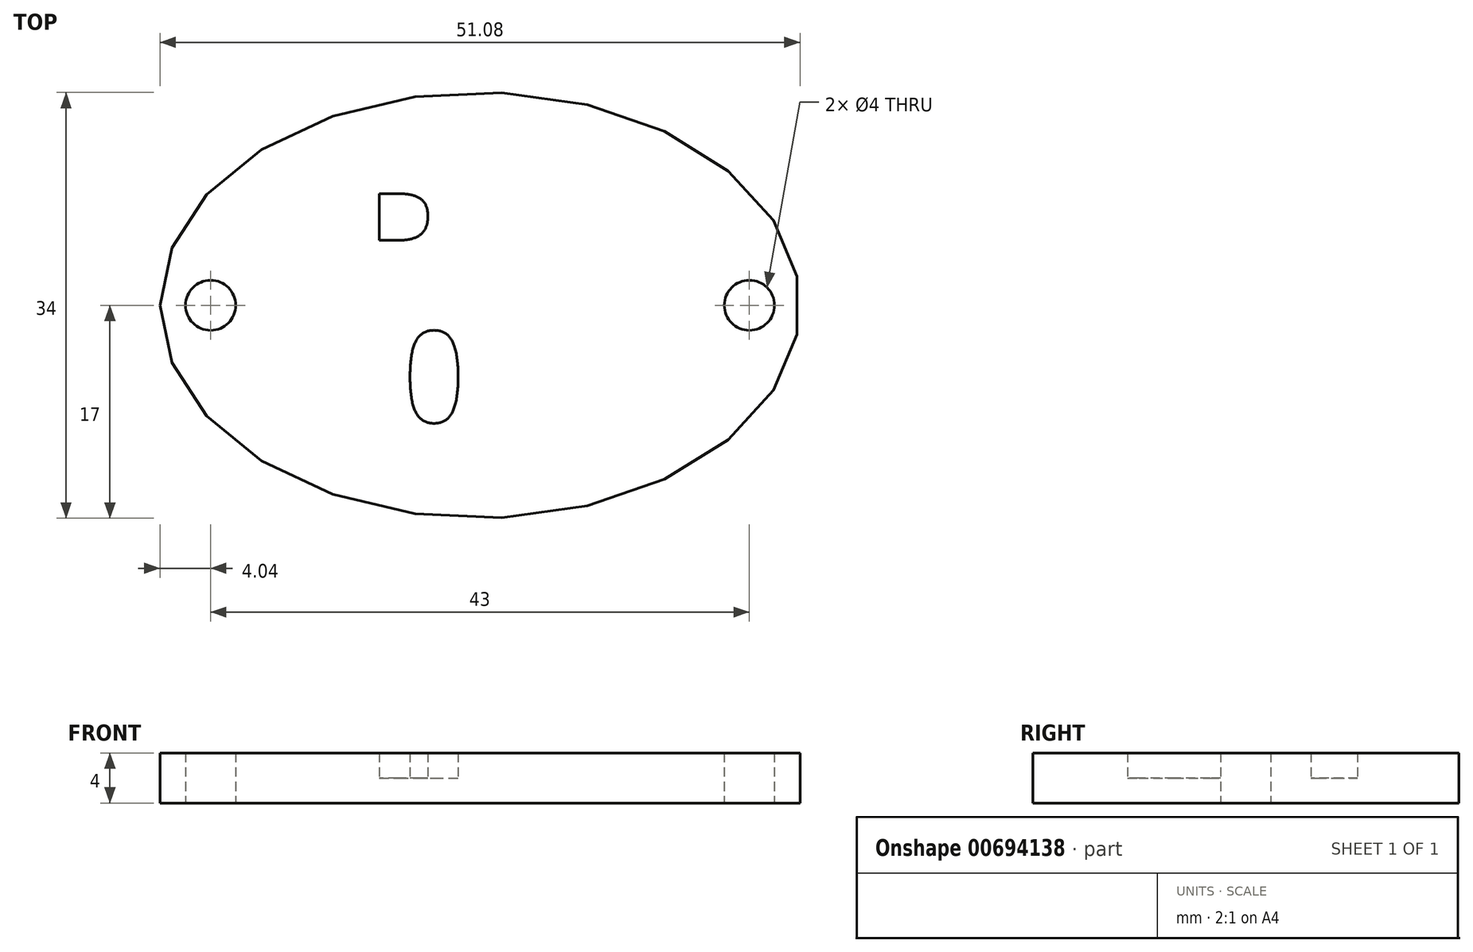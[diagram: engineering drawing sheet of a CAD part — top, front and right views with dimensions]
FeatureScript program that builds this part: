
annotation { "Feature Type Name" : "Feature", "Feature Type Description" : "" }
export const myFeature = defineFeature(function(context is Context, id is Id, definition is map)
    precondition{}
    {
        {
            var Q0;
            Q0=qCreatedBy(makeId("Top.planeOp"),FACE);
            var sketch = newSketch(context, id + "F0", { "sketchPlane" : qUnion([Q0])});
            skLineSegment(sketch, "E0", {"start": v(0, 0) * mm, "end": v(-21.5, 0) * mm, "construction": true});
            skCircle(sketch, "E1", {"center": v(-21.5, 0) * mm, "radius": 2 * mm});
            skLineSegment(sketch, "E2", {"start": v(0, 0) * mm, "end": v(0, 17) * mm, "construction": true});
            skArc(sketch, "E3", {"start": v(-20.06, -3.73) * mm, "mid": v(-17.5, 0) * mm, "end": v(-20.06, 3.73) * mm});
            skEllipse(sketch, "E4", {"center": v(0, 0) * mm, "majorRadius": 17 * mm, "minorRadius": 25.54 * mm, "majorAxis": v(0, 1)});
            skArc(sketch, "E5.MirrorC", {"start": v(20.06, -3.73) * mm, "mid": v(17.5, 0) * mm, "end": v(20.06, 3.73) * mm});
            skCircle(sketch, "E6.MirrorC", {"center": v(21.5, 0) * mm, "radius": 2 * mm});
            skFitSpline(sketch, "E7.0", {"points": [v(-23.47, 1.39) * mm, v(-23.57, 0) * mm, v(-23.47, -1.39) * mm, v(-23.16, -2.76) * mm, v(-22.65, -4.12) * mm, v(-21.93, -5.45) * mm, v(-21, -6.76) * mm, v(-19.87, -8.03) * mm, v(-18.75, -9.03) * mm, v(-17.76, -9.8) * mm, v(-16.96, -10.36) * mm, v(-16.11, -10.9) * mm, v(-14.94, -11.57) * mm, v(-13.38, -12.34) * mm, v(-11.38, -13.13) * mm, v(-9.26, -13.8) * mm, v(-7.04, -14.33) * mm, v(-4.75, -14.71) * mm, v(-2.8, -14.9) * mm, v(-1.2, -14.99) * mm, v(0, -15) * mm, v(1.2, -14.99) * mm, v(2.8, -14.9) * mm, v(4.75, -14.71) * mm, v(7.04, -14.33) * mm, v(9.26, -13.8) * mm, v(11.38, -13.13) * mm, v(13.38, -12.34) * mm, v(14.94, -11.57) * mm, v(16.11, -10.9) * mm, v(16.96, -10.36) * mm, v(17.76, -9.8) * mm, v(18.75, -9.03) * mm, v(19.87, -8.03) * mm, v(21, -6.76) * mm, v(21.93, -5.45) * mm, v(22.65, -4.12) * mm, v(23.16, -2.76) * mm, v(23.47, -1.39) * mm, v(23.57, 0) * mm, v(23.47, 1.39) * mm, v(23.16, 2.76) * mm, v(22.65, 4.12) * mm, v(21.93, 5.45) * mm, v(21, 6.76) * mm, v(19.87, 8.03) * mm, v(18.75, 9.03) * mm, v(17.76, 9.8) * mm, v(16.96, 10.36) * mm, v(16.11, 10.9) * mm, v(14.94, 11.57) * mm, v(13.38, 12.34) * mm, v(11.38, 13.13) * mm, v(9.26, 13.8) * mm, v(7.04, 14.33) * mm, v(4.75, 14.71) * mm, v(2.8, 14.9) * mm, v(1.2, 14.99) * mm, v(0, 15) * mm, v(-1.2, 14.99) * mm, v(-2.8, 14.9) * mm, v(-4.75, 14.71) * mm, v(-7.04, 14.33) * mm, v(-9.26, 13.8) * mm, v(-11.38, 13.13) * mm, v(-13.38, 12.34) * mm, v(-14.94, 11.57) * mm, v(-16.11, 10.9) * mm, v(-16.96, 10.36) * mm, v(-17.76, 9.8) * mm, v(-18.75, 9.03) * mm, v(-19.87, 8.03) * mm, v(-21, 6.76) * mm, v(-21.93, 5.45) * mm, v(-22.65, 4.12) * mm, v(-23.16, 2.76) * mm, v(-23.47, 1.39) * mm, v(-23.57, 0) * mm, v(-23.47, -1.39) * mm]});
            skFitSpline(sketch, "E8.trimOffspring", {"points": [v(-23.47, 1.39) * mm, v(-23.57, 0) * mm, v(-23.47, -1.39) * mm, v(-23.16, -2.76) * mm, v(-22.65, -4.12) * mm, v(-21.93, -5.45) * mm, v(-21, -6.76) * mm, v(-19.87, -8.03) * mm, v(-18.75, -9.03) * mm, v(-17.76, -9.8) * mm, v(-16.96, -10.36) * mm, v(-16.11, -10.9) * mm, v(-14.94, -11.57) * mm, v(-13.38, -12.34) * mm, v(-11.38, -13.13) * mm, v(-9.26, -13.8) * mm, v(-7.04, -14.33) * mm, v(-4.75, -14.71) * mm, v(-2.8, -14.9) * mm, v(-1.2, -14.99) * mm, v(0, -15) * mm, v(1.2, -14.99) * mm, v(2.8, -14.9) * mm, v(4.75, -14.71) * mm, v(7.04, -14.33) * mm, v(9.26, -13.8) * mm, v(11.38, -13.13) * mm, v(13.38, -12.34) * mm, v(14.94, -11.57) * mm, v(16.11, -10.9) * mm, v(16.96, -10.36) * mm, v(17.76, -9.8) * mm, v(18.75, -9.03) * mm, v(19.87, -8.03) * mm, v(21, -6.76) * mm, v(21.93, -5.45) * mm, v(22.65, -4.12) * mm, v(23.16, -2.76) * mm, v(23.47, -1.39) * mm, v(23.57, 0) * mm, v(23.47, 1.39) * mm, v(23.16, 2.76) * mm, v(22.65, 4.12) * mm, v(21.93, 5.45) * mm, v(21, 6.76) * mm, v(19.87, 8.03) * mm, v(18.75, 9.03) * mm, v(17.76, 9.8) * mm, v(16.96, 10.36) * mm, v(16.11, 10.9) * mm, v(14.94, 11.57) * mm, v(13.38, 12.34) * mm, v(11.38, 13.13) * mm, v(9.26, 13.8) * mm, v(7.04, 14.33) * mm, v(4.75, 14.71) * mm, v(2.8, 14.9) * mm, v(1.2, 14.99) * mm, v(0, 15) * mm, v(-1.2, 14.99) * mm, v(-2.8, 14.9) * mm, v(-4.75, 14.71) * mm, v(-7.04, 14.33) * mm, v(-9.26, 13.8) * mm, v(-11.38, 13.13) * mm, v(-13.38, 12.34) * mm, v(-14.94, 11.57) * mm, v(-16.11, 10.9) * mm, v(-16.96, 10.36) * mm, v(-17.76, 9.8) * mm, v(-18.75, 9.03) * mm, v(-19.87, 8.03) * mm, v(-21, 6.76) * mm, v(-21.93, 5.45) * mm, v(-22.65, 4.12) * mm, v(-23.16, 2.76) * mm, v(-23.47, 1.39) * mm, v(-23.57, 0) * mm, v(-23.47, -1.39) * mm]});
            skArc(sketch, "E9.filletArc", {"start": v(-20.88, 6.86) * mm, "mid": v(-21.27, 5.09) * mm, "end": v(-20.06, 3.73) * mm});
            skArc(sketch, "E10.filletArc", {"start": v(-20.06, -3.73) * mm, "mid": v(-21.27, -5.09) * mm, "end": v(-20.88, -6.86) * mm});
            skArc(sketch, "E11.filletArc", {"start": v(20.88, -6.86) * mm, "mid": v(21.27, -5.09) * mm, "end": v(20.06, -3.73) * mm});
            skArc(sketch, "E12.filletArc", {"start": v(20.06, 3.73) * mm, "mid": v(21.27, 5.09) * mm, "end": v(20.88, 6.86) * mm});
            skText(sketch, "E13", { "text": "SRMS", "fontName": "OpenSans-Regular.ttf"});
            skText(sketch, "E14", { "text": "2017", "fontName": "OpenSans-Regular.ttf"});
            const initialGuessF0  = {"E13": [-0.018, 0.00017, 1, 0, 0.00983], "E14": [-0.01438, -0.01018, 1, 0, 0.009]};
            skSetInitialGuess(sketch, initialGuessF0);
            skSolve(sketch);
        }
        {
            var Q0;
            Q0=qCreatedBy(makeId("Top.planeOp"),FACE);
            var sketch = newSketch(context, id + "F1", { "sketchPlane" : qUnion([Q0])});
            skLineSegment(sketch, "E15", {"start": v(0, 0) * mm, "end": v(-21.5, 0) * mm, "construction": true});
            skCircle(sketch, "E16", {"center": v(-21.5, 0) * mm, "radius": 2 * mm});
            skLineSegment(sketch, "E17", {"start": v(0, 0) * mm, "end": v(0, 17) * mm, "construction": true});
            skEllipse(sketch, "E18", {"center": v(0, 0) * mm, "majorRadius": 17 * mm, "minorRadius": 25.54 * mm, "majorAxis": v(0, 1)});
            skCircle(sketch, "E19.MirrorC", {"center": v(21.5, 0) * mm, "radius": 2 * mm});
            skSolve(sketch);
        }
        {
            var Q0;
            Q0=makeQuery(id+"F1.imprint","IMPRINT",FACE,{"disambiguationData":[TD([[makeQuery(id+"F1.imprint","IMPRINT",EDGE,{"derivedFrom":sQuery(id+"F1.wireOp",EDGE,"E16")}),-1.0]])]});
            extrude(context, id + "F2", {"entities" : qUnion([Q0]), "depth" : 4 * mm, "offsetDistance" : 25 * mm});
        }
        {
            var Q0;
            Q0=makeQuery(id+"F0.imprint","IMPRINT",FACE,{"disambiguationData":[TD([[makeQuery(id+"F0.imprint","IMPRINT",EDGE,{"derivedFrom":sQuery(id+"F0.wireOp",EDGE,"E3")}),-1.0]])]});
            var Q1;
            Q1=makeQuery(id+"F0.imprint","IMPRINT",FACE,{"disambiguationData":[TD([[makeQuery(id+"F0.imprint","IMPRINT",EDGE,{"derivedFrom":sQuery(id+"F0.wireOp",EDGE,"E13.sketch_text.stroke-36")}),1.0]])]});
            var Q2;
            Q2=makeQuery(id+"F0.imprint","IMPRINT",FACE,{"disambiguationData":[TD([[makeQuery(id+"F0.imprint","IMPRINT",EDGE,{"derivedFrom":sQuery(id+"F0.wireOp",EDGE,"E14.sketch_text.stroke-28")}),1.0]])]});
            extrude(context, id + "F3", {"entities" : qUnion([Q0, Q1, Q2]), "operationType" : NewBodyOperationType.REMOVE, "depth" : 25 * mm, "offsetDistance" : 25 * mm, "hasSecondDirection" : true, "secondDirectionOppositeDirection" : false, "secondDirectionDepth" : 2 * mm});
        }
    });
